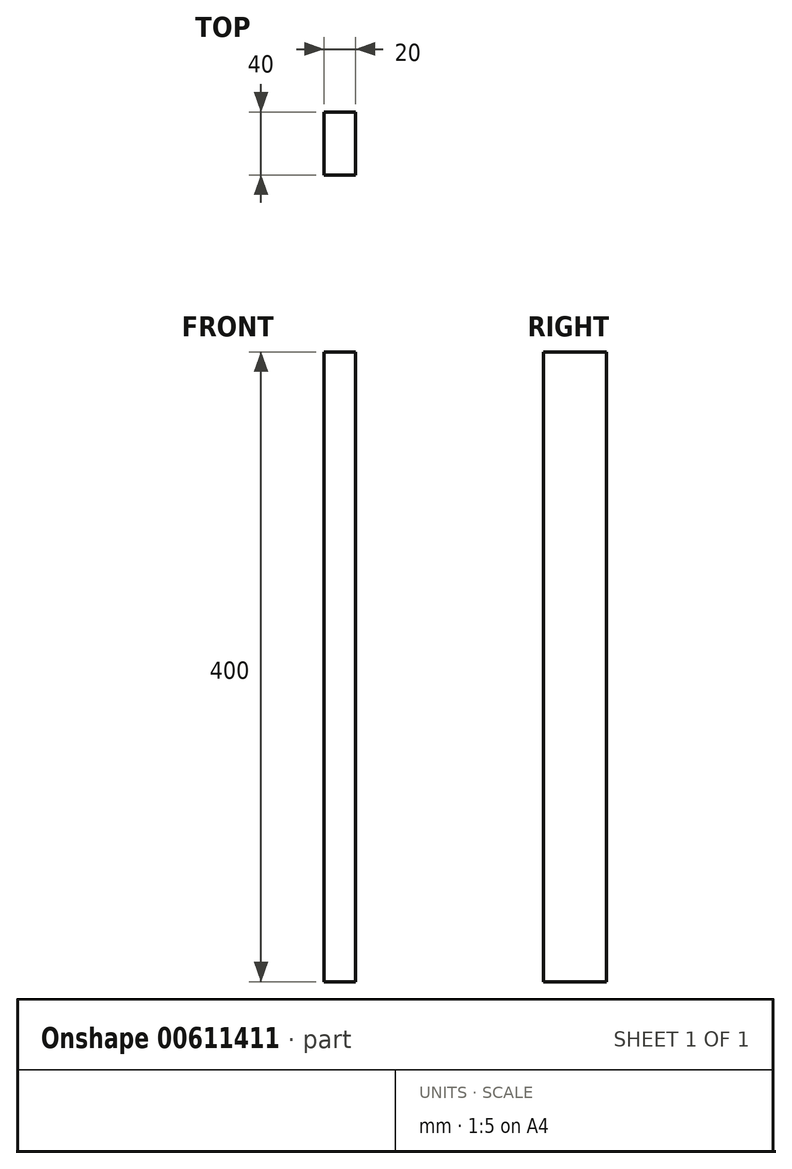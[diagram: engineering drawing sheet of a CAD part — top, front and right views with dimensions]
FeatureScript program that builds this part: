
annotation { "Feature Type Name" : "Feature", "Feature Type Description" : "" }
export const myFeature = defineFeature(function(context is Context, id is Id, definition is map)
    precondition{}
    {
        {
            var Q0;
            Q0=qCreatedBy(makeId("Top.planeOp"),FACE);
            var sketch = newSketch(context, id + "F0", { "sketchPlane" : qUnion([Q0])});
            skLineSegment(sketch, "E0.bottom", {"start": v(10, 20) * mm, "end": v(-10, 20) * mm});
            skLineSegment(sketch, "E0.top", {"start": v(10, -20) * mm, "end": v(-10, -20) * mm});
            skLineSegment(sketch, "E0.left", {"start": v(10, 20) * mm, "end": v(10, -20) * mm});
            skLineSegment(sketch, "E0.right", {"start": v(-10, 20) * mm, "end": v(-10, -20) * mm});
            skPoint(sketch, "E0.middle", {"position": v(0, 0) * mm});
            skSolve(sketch);
        }
        {
            var Q0;
            Q0=makeQuery(id+"F0.imprint","IMPRINT",FACE,{"disambiguationData":[TD([[makeQuery(id+"F0.imprint","IMPRINT",EDGE,{"derivedFrom":sQuery(id+"F0.wireOp",EDGE,"E0.bottom")}),1.0]])]});
            extrude(context, id + "F1", {"entities" : qUnion([Q0]), "depth" : 400 * mm, "offsetDistance" : 25 * mm});
        }
    });
